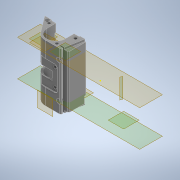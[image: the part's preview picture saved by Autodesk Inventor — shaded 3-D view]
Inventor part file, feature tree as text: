
AUTODESK INVENTOR PART (.ipt)
format: ipt  version: 2022 (Build 260153000, 153)  size: 1,463,808 bytes
history: native  units: mm
features: sketch x41, extrude x39, reference x39, projected_geometry x32, other x31, fillet x27, chamfer x4, mirror x2
ambient origin geometry x8: Origin, YZ Plane, XZ Plane, XY Plane, X Axis, Y Axis, Z Axis, Center Point
bodies: Body1 (feature_tree)
feature tree (215):
  other  "Твердое тело1"
  extrude  "Выдавливание1"  Depth=3.0mm
  extrude  "Выдавливание3"  Depth=3.0mm
  other  "РабПлоскость3"
  extrude  "Выдавливание4"  Depth=0.5mm
  other  "РабПлоскость6"
  extrude  "Выдавливание5"  Depth=0.5mm
  other  "РабПлоскость2"
  extrude  "Выдавливание6"  Depth=150.0mm
  fillet  "Сопряжение1"  Radius=81.0mm
  extrude  "Выдавливание7"  Depth=14.0mm TaperAngle=0.0deg
  chamfer  "Фаска2"  Distance=14.0mm
  extrude  "Выдавливание8"  Depth=2.0mm
  mirror  "Зеркальное отражение2"
  sketch  "Эскиз11"
  extrude  "Выдавливание10"  Depth=2.0mm
  extrude  "Выдавливание11"  TaperAngle=0.0deg  [1 undecoded]
  extrude  "Выдавливание12"  Depth=2.0mm
  extrude  "Выдавливание13"  Depth=65.0mm
  extrude  "Выдавливание14"  Depth=2.2mm
  extrude  "Выдавливание15"  Depth=10.0mm TaperAngle=0.0deg
  extrude  "Выдавливание16"  Depth=300.0mm TaperAngle=0.0deg
  extrude  "Выдавливание17"  Depth=41.0mm
  fillet  "Сопряжение2"  Radius=81.0mm
  fillet  "Сопряжение3"  Radius=30.0mm
  fillet  "Сопряжение4"  Radius=30.0mm
  sketch  "Эскиз21"
  extrude  "Выдавливание21"  Depth=2.0mm
  fillet  "Сопряжение7"  Radius=3.0mm
  other  "РабПлоскость7"
  extrude  "Выдавливание22"  Depth=15.0mm
  extrude  "Выдавливание23"  Depth=15.0mm
  other  "РабПлоскость8"
  extrude  "Выдавливание24"  Depth=3.2mm
  mirror  "Зеркальное отражение6"
  chamfer  "Фаска4"  Distance=3.2mm
  fillet  "Сопряжение9"  Radius=50.0mm
  extrude  "Выдавливание31"  Depth=1.8mm TaperAngle=45.0deg
  chamfer  "Фаска5"  Distance=4.2mm
  other  "РабПлоскость13"
  other  "РабПлоскость11"
  extrude  "Выдавливание35"  Depth=4.0mm
  extrude  "Выдавливание36"  Depth=4.0mm
  extrude  "Выдавливание37"  Depth=6.0mm TaperAngle=0.0deg
  other  "РабПлоскость12"
  extrude  "Выдавливание38"  Depth=4.2mm
  extrude  "Выдавливание39"  Depth=4.2mm
  fillet  "Сопряжение14"  Radius=4.2mm
  fillet  "Сопряжение15"  Radius=4.2mm
  fillet  "Сопряжение16"  Radius=8.0mm
  extrude  "Выдавливание40"  Depth=4.2mm
  extrude  "Выдавливание41"  Depth=4.2mm
  extrude  "Выдавливание42"  Depth=8.0mm TaperAngle=0.0deg
  fillet  "Сопряжение17"  Radius=25.0mm
  fillet  "Сопряжение18"  Radius=4.2mm
  extrude  "Выдавливание43"  Depth=4.2mm
  fillet  "Сопряжение19"  Radius=6.0mm
  fillet  "Сопряжение20"  Radius=20.0mm
  fillet  "Сопряжение21"  Radius=10.0mm
  fillet  "Сопряжение22"  Radius=1.5mm
  extrude  "Выдавливание44"  Depth=0.3mm
  extrude  "Выдавливание45"  Depth=0.3mm
  fillet  "Сопряжение23"  Radius=0.3mm
  fillet  "Сопряжение24"  Radius=8.5mm
  extrude  "Выдавливание46"  Depth=4.95mm
  fillet  "Сопряжение25"  Radius=0.3mm
  extrude  "Выдавливание47"  Depth=2.0mm
  fillet  "Сопряжение26"  Radius=3.0mm
  extrude  "Выдавливание48"  Depth=25.0mm
  fillet  "Сопряжение27"  Radius=1.0mm
  extrude  "Выдавливание49"  Depth=0.5mm
  chamfer  "Фаска6"  Distance=0.5mm
  fillet  "Сопряжение28"  Radius=25.0mm
  fillet  "Сопряжение29"  Radius=1.7mm
  extrude  "Выдавливание50"  Depth=35.0mm TaperAngle=0.0deg
  fillet  "Сопряжение30"  Radius=11.0mm
  fillet  "Сопряжение31"  Radius=35.0mm
  fillet  "Сопряжение32"  Radius=12.0mm
  extrude  "Выдавливание51"  Depth=0.3mm
  fillet  "Сопряжение33"  Radius=1.0mm
  extrude  "Выдавливание52"  Depth=1.0mm
  fillet  "Сопряжение36"  Radius=2.0mm
  extrude  "Выдавливание53"  Depth=0.5mm
  sketch  "Эскиз1"
  reference  "Ссылка1"
  reference  "Ссылка2"
  reference  "Ссылка3"
  reference  "Ссылка4"
  reference  "Ссылка5"
  reference  "Ссылка6"
  reference  "Ссылка7"
  reference  "Ссылка8"
  reference  "Ссылка9"
  sketch  "Эскиз4"
  sketch  "Эскиз5"
  sketch  "Эскиз6"
  sketch  "Эскиз7"
  projected_geometry  "Спроецированная петля5"
  projected_geometry  "Спроецированная петля6"
  sketch  "Эскиз8"
  reference  "Ссылка17"
  projected_geometry  "Спроецированная петля7"
  sketch  "Эскиз9"
  reference  "Ссылка18"
  reference  "Ссылка19"
  reference  "Ссылка20"
  sketch  "Эскиз12"
  reference  "Ссылка23"
  sketch  "Эскиз13"
  sketch  "Эскиз15"
  projected_geometry  "Спроецированная петля13"
  sketch  "Эскиз16"
  projected_geometry  "Спроецированная петля14"
  projected_geometry  "Спроецированная петля15"
  projected_geometry  "Спроецированная петля16"
  sketch  "Эскиз17"
  reference  "Ссылка24"
  reference  "Ссылка25"
  sketch  "Эскиз18"
  projected_geometry  "Спроецированная петля19"
  sketch  "Эскиз19"
  projected_geometry  "Спроецированная петля20"
  sketch  "Эскиз20"
  projected_geometry  "Спроецированная петля21"
  projected_geometry  "Спроецированная петля22"
  projected_geometry  "Спроецированная петля23"
  projected_geometry  "Спроецированная петля24"
  sketch  "Эскиз25"
  reference  "Ссылка27"
  reference  "Ссылка28"
  reference  "Ссылка29"
  sketch  "Эскиз26"
  reference  "Ссылка30"
  reference  "Ссылка31"
  sketch  "Эскиз27"
  projected_geometry  "Спроецированная петля28"
  sketch  "Эскиз28"
  projected_geometry  "Спроецированная петля29"
  reference  "Ссылка32"
  reference  "Ссылка33"
  reference  "Ссылка34"
  other  "РабПлоскость9"
  sketch  "Эскиз36"
  projected_geometry  "Спроецированная петля37"
  projected_geometry  "Спроецированная петля38"
  reference  "Ссылка42"
  reference  "Ссылка43"
  sketch  "Эскиз39"
  reference  "Ссылка45"
  sketch  "Эскиз40"
  projected_geometry  "Спроецированная петля41"
  reference  "Ссылка46"
  reference  "Ссылка47"
  sketch  "Эскиз41"
  reference  "Ссылка48"
  reference  "Ссылка49"
  reference  "Ссылка50"
  sketch  "Эскиз42"
  reference  "Ссылка51"
  projected_geometry  "Спроецированная петля42"
  sketch  "Эскиз43"
  projected_geometry  "Спроецированная петля43"
  sketch  "Эскиз44"
  reference  "Ссылка52"
  sketch  "Эскиз45"
  reference  "Ссылка53"
  reference  "Ссылка54"
  sketch  "Эскиз46"
  projected_geometry  "Спроецированная петля44"
  sketch  "Эскиз47"
  projected_geometry  "Спроецированная петля45"
  projected_geometry  "Спроецированная петля46"
  sketch  "Эскиз48"
  projected_geometry  "Спроецированная петля47"
  sketch  "Эскиз49"
  sketch  "Эскиз50"
  projected_geometry  "Спроецированная петля48"
  projected_geometry  "Спроецированная петля49"
  sketch  "Эскиз51"
  projected_geometry  "Спроецированная петля50"
  sketch  "Эскиз52"
  projected_geometry  "Спроецированная петля51"
  sketch  "Эскиз53"
  projected_geometry  "Спроецированная петля52"
  projected_geometry  "Спроецированная петля53"
  reference  "Ссылка55"
  sketch  "Эскиз54"
  reference  "Ссылка56"
  reference  "Ссылка57"
  sketch  "Эскиз55"
  projected_geometry  "Спроецированная петля54"
  sketch  "Эскиз56"
  projected_geometry  "Спроецированная петля55"
  sketch  "Эскиз57"
  other  "<userpath>\Documents\Git\MZCAT_2024\MZCAT.iam"
  other  "MZCAT.iam"
  other  "plan:1"
  other  "akkum_plate:1"
  other  "main_wheel_fixator:1"
  other  "CAT_protector:1"
  other  "base plate:2"
  other  "<userpath>\Documents\Git\MZCAT_2024\MZCAT_4.iam"
  other  "MZCAT_4.iam"
  other  "OCS-D008 B:1"
  other  "Linit Switch:2"
  other  "Linit Switch:1"
  other  "concevik:1"
  other  "FastBattery:1"
  other  "metal_cap:1"
  other  "vydacha_slide:1"
  other  "motherboard_plate:1"
  other  "cable_slide2:1"
  other  "cable_slide:1"
  other  "upor:1"
  other  "<userpath>\Documents\Git\MZCAT_2024\MZCAT_4.iam"
note: 1 required parameter value undecoded (feature->parameter linkage not recoverable at this tier; creation-order binding heuristic only, values carry confidence <= 0.55)
